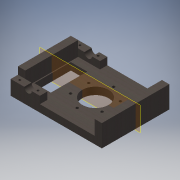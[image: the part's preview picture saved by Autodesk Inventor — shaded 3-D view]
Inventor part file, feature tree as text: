
AUTODESK INVENTOR PART (.ipt)
format: ipt  version: 2019.3 (Build 233278000, 278)  size: 223,232 bytes
history: native  units: in
note: dims shown in document units (in); Inventor stores cm internally (conversion verified against a paired STEP export)
features: sketch x9, extrude x7, hole x2, projected_geometry x2, pattern_circular x1, mirror x1
ambient origin geometry x8: Origin, YZ Plane, XZ Plane, XY Plane, X Axis, Y Axis, Z Axis, Center Point
bodies: Body1 (feature_tree)
feature tree (22):
  extrude  "Extrusion5"  Depth=1.8in
  hole  "Hole4"  [1 undecoded]
  pattern_circular  "Circular Pattern1"  Count=6 Angle=360.0deg
  extrude  "Extrusion6"  Depth=2.0in
  mirror  "Mirror2"
  extrude  "Extrusion7"  Depth=0.5in
  extrude  "Extrusion8"  Depth=0.5in
  extrude  "Extrusion9"  Depth=0.5in
  extrude  "Extrusion10"  Depth=1.0in TaperAngle=0.0deg
  hole  "Hole6"  [1 undecoded]
  extrude  "Extrusion11"  Depth=0.5in
  sketch  "Sketch10"  dims[d56=7.0in d57=1.8in]
  sketch  "Sketch11"  dims[d58=0.5in d59=0.0in d60=1.25in]
  sketch  "Sketch12"  dims[d61=0.104in d62=0.276in d63=0.185in d64=0.281in d65=0.5635in d66=1.0in d67=0.8108in d68=2.3622in d69=360.0deg]
  sketch  "Sketch13"  dims[d71=0.5in d72=2.0in]
  sketch  "Sketch14"  dims[d73=0.5in d74=0.0in d75=0.52in]
  sketch  "Sketch15"  dims[d76=1.0in d77=0.0in d78=0.5in]
  sketch  "Sketch16"  dims[d79=1.0in d80=0.0in d81=0.5in]
  sketch  "Sketch18"  dims[d82=5.75in d83=1.0in d84=0.0in]
  projected_geometry  "Projected Loop1"
  projected_geometry  "Projected Loop2"
  sketch  "Sketch19"  dims[d85=1.0in d86=0.0in d94=0.375in d95=0.375in d96=0.15in d97=0.276in d98=0.279in d99=0.25in d100=0.5635in d101=1.0in d102=0.8108in d103=0.5in d104=0.0in]
note: 2 required parameter values undecoded (feature->parameter linkage not recoverable at this tier; creation-order binding heuristic only, values carry confidence <= 0.55)
